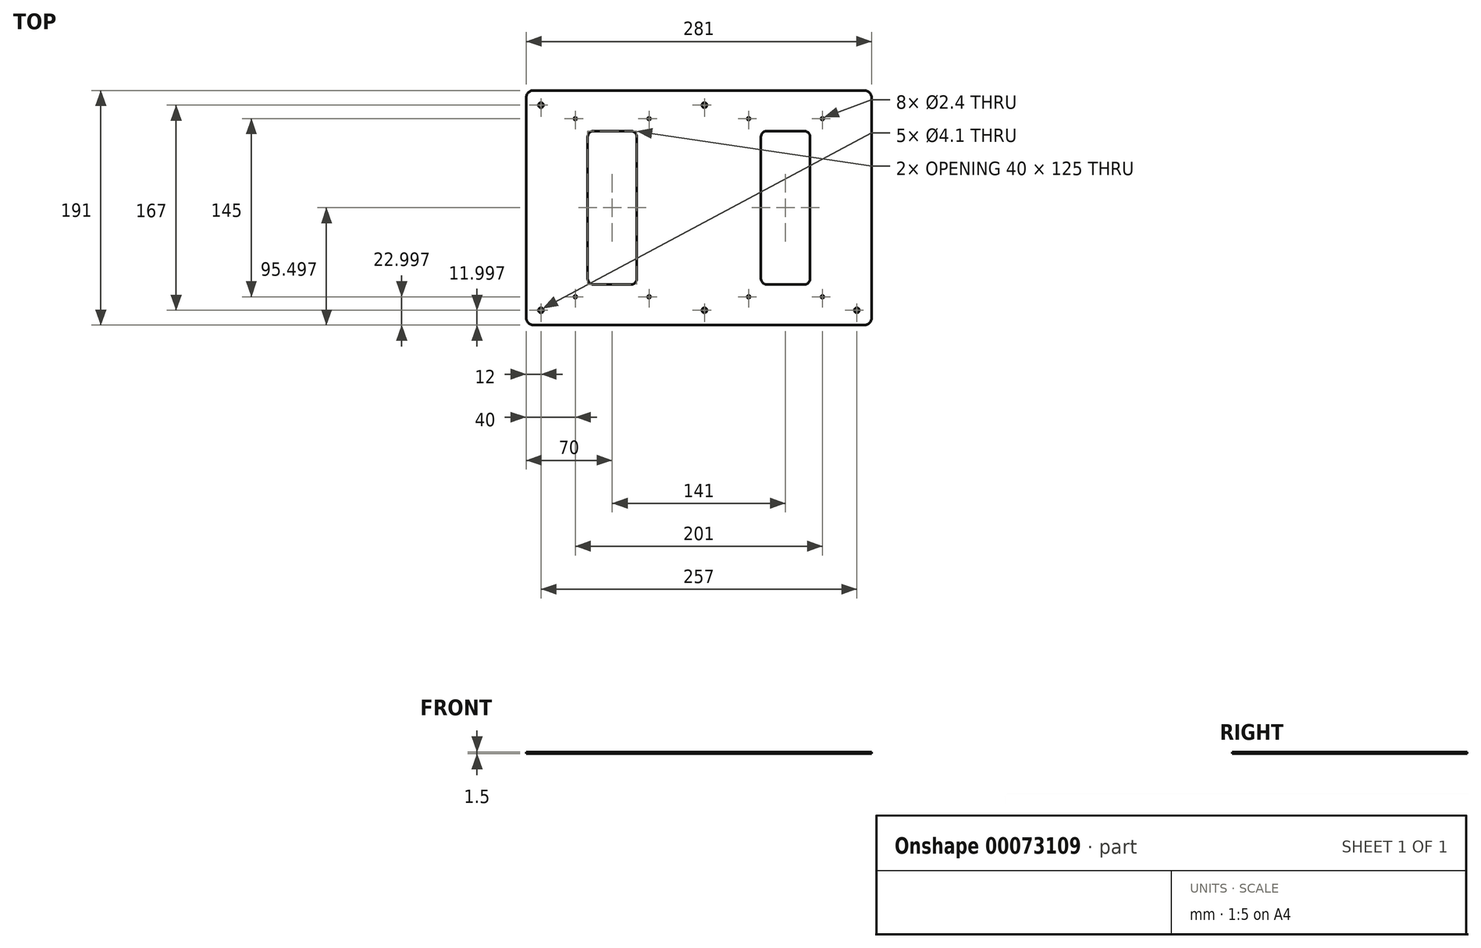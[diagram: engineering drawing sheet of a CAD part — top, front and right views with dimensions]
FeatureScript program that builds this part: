
annotation { "Feature Type Name" : "Feature", "Feature Type Description" : "" }
export const myFeature = defineFeature(function(context is Context, id is Id, definition is map)
    precondition{}
    {
        {
            var Q0;
            Q0=qCreatedBy(makeId("Top.planeOp"),FACE);
            var sketch = newSketch(context, id + "F0", { "sketchPlane" : qUnion([Q0])});
            skLineSegment(sketch, "E0.rect.bottom", {"start": v(-126, 99.25) * mm, "end": v(155, 99.25) * mm});
            skLineSegment(sketch, "E0.rect.top", {"start": v(-126, -91.75) * mm, "end": v(155, -91.75) * mm});
            skLineSegment(sketch, "E0.rect.left", {"start": v(-126, 99.25) * mm, "end": v(-126, -91.75) * mm});
            skLineSegment(sketch, "E0.rect.right", {"start": v(155, 99.25) * mm, "end": v(155, -91.75) * mm});
            skPoint(sketch, "E1", {"position": v(-114, 87.25) * mm});
            skPoint(sketch, "E2", {"position": v(19, 87.25) * mm});
            skPoint(sketch, "E3", {"position": v(143, -79.75) * mm});
            skPoint(sketch, "E4", {"position": v(-114, -79.75) * mm});
            skPoint(sketch, "E5", {"position": v(19, -79.75) * mm});
            skLineSegment(sketch, "E6", {"start": v(-126, 3.75) * mm, "end": v(155, 3.75) * mm, "construction": true});
            skPoint(sketch, "E7", {"position": v(-86, 76.25) * mm});
            skPoint(sketch, "E8", {"position": v(-86, -68.75) * mm});
            skPoint(sketch, "E9", {"position": v(-26, -68.75) * mm});
            skPoint(sketch, "E10", {"position": v(-26, 76.25) * mm});
            skLineSegment(sketch, "E11.bottom", {"start": v(-71, 66.25) * mm, "end": v(-41, 66.25) * mm});
            skLineSegment(sketch, "E11.top", {"start": v(-71, -58.75) * mm, "end": v(-41, -58.75) * mm});
            skLineSegment(sketch, "E11.left", {"start": v(-76, 61.25) * mm, "end": v(-76, -53.75) * mm});
            skLineSegment(sketch, "E11.right", {"start": v(-36, 61.25) * mm, "end": v(-36, -53.75) * mm});
            skPoint(sketch, "E12.visualSharp", {"position": v(-76, 66.25) * mm});
            skArc(sketch, "E12.filletArc", {"start": v(-71, 66.25) * mm, "mid": v(-74.54, 64.78) * mm, "end": v(-76, 61.25) * mm});
            skPoint(sketch, "E13.visualSharp", {"position": v(-36, 66.25) * mm});
            skArc(sketch, "E13.filletArc", {"start": v(-36, 61.25) * mm, "mid": v(-37.46, 64.78) * mm, "end": v(-41, 66.25) * mm});
            skPoint(sketch, "E14.visualSharp", {"position": v(-76, -58.75) * mm});
            skArc(sketch, "E14.filletArc", {"start": v(-76, -53.75) * mm, "mid": v(-74.54, -57.29) * mm, "end": v(-71, -58.75) * mm});
            skPoint(sketch, "E15.visualSharp", {"position": v(-36, -58.75) * mm});
            skArc(sketch, "E15.filletArc", {"start": v(-41, -58.75) * mm, "mid": v(-37.46, -57.29) * mm, "end": v(-36, -53.75) * mm});
            skLineSegment(sketch, "E16", {"start": v(14.5, 99.25) * mm, "end": v(14.5, -195.72) * mm, "construction": true});
            skPoint(sketch, "E17.MirrorP", {"position": v(55, -68.75) * mm});
            skPoint(sketch, "E18.MirrorP", {"position": v(115, -68.75) * mm});
            skArc(sketch, "E19.MirrorCS", {"start": v(105, -53.75) * mm, "mid": v(103.54, -57.29) * mm, "end": v(100, -58.75) * mm});
            skArc(sketch, "E20.MirrorCS", {"start": v(70, -58.75) * mm, "mid": v(66.46, -57.29) * mm, "end": v(65, -53.75) * mm});
            skPoint(sketch, "E21.MirrorP", {"position": v(105, -58.75) * mm});
            skLineSegment(sketch, "E22.MirrorCS", {"start": v(105, 61.25) * mm, "end": v(105, -53.75) * mm});
            skPoint(sketch, "E23.MirrorP", {"position": v(65, -58.75) * mm});
            skLineSegment(sketch, "E24.MirrorCS", {"start": v(65, 61.25) * mm, "end": v(65, -53.75) * mm});
            skLineSegment(sketch, "E25.MirrorCS", {"start": v(100, -58.75) * mm, "end": v(70, -58.75) * mm});
            skArc(sketch, "E26.MirrorCS", {"start": v(65, 61.25) * mm, "mid": v(66.46, 64.78) * mm, "end": v(70, 66.25) * mm});
            skArc(sketch, "E27.MirrorCS", {"start": v(100, 66.25) * mm, "mid": v(103.54, 64.78) * mm, "end": v(105, 61.25) * mm});
            skPoint(sketch, "E28.MirrorP", {"position": v(105, 66.25) * mm});
            skPoint(sketch, "E29.MirrorP", {"position": v(65, 66.25) * mm});
            skLineSegment(sketch, "E30.MirrorCS", {"start": v(100, 66.25) * mm, "end": v(70, 66.25) * mm});
            skPoint(sketch, "E31.MirrorP", {"position": v(115, 76.25) * mm});
            skPoint(sketch, "E32.MirrorP", {"position": v(55, 76.25) * mm});
            skLineSegment(sketch, "E33.trimOffspring", {"start": v(30.5, -91.75) * mm, "end": v(30.5, -195.72) * mm});
            skLineSegment(sketch, "E34.trimOffspring", {"start": v(-1.5, -91.75) * mm, "end": v(-1.5, -195.72) * mm});
            skPoint(sketch, "E35", {"position": v(-1.5, 19.75) * mm});
            skPoint(sketch, "E36", {"position": v(30.5, 19.75) * mm});
            skPoint(sketch, "E37", {"position": v(30.5, -12.25) * mm});
            skPoint(sketch, "E38", {"position": v(-1.5, -12.25) * mm});
            skPoint(sketch, "E39", {"position": v(14.5, 3.75) * mm});
            skSolve(sketch);
        }
        {
            var Q0;
            Q0=makeQuery(id+"F0.imprint","IMPRINT",FACE,{"disambiguationData":[TD([[makeQuery(id+"F0.imprint","IMPRINT",EDGE,{"derivedFrom":sQuery(id+"F0.wireOp",EDGE,"E0.rect.bottom")}),-1.0]])]});
            extrude(context, id + "F1", {"entities" : qUnion([Q0]), "depth" : 1.5 * mm});
        }
        {
            var Q0;
            Q0=sQuery(id+"F0.wireOp",VERTEX,"E1");
            var Q1;
            Q1=sQuery(id+"F0.wireOp",VERTEX,"E2");
            var Q2;
            Q2=sQuery(id+"F0.wireOp",VERTEX,"E3");
            var Q3;
            Q3=sQuery(id+"F0.wireOp",VERTEX,"E4");
            var Q4;
            Q4=sQuery(id+"F0.wireOp",VERTEX,"E5");
            var Q5;
            Q5=makeQuery(id+"F1.opExtrude","SWEPT_BODY",BODY,{"disambiguationData":[OSD([sQuery(id+"F0.wireOp",EDGE,"E0.rect.bottom"),sQuery(id+"F0.wireOp",EDGE,"E0.rect.top"),sQuery(id+"F0.wireOp",EDGE,"E0.rect.left"),sQuery(id+"F0.wireOp",EDGE,"E0.rect.right")])]});
            hole(context, id + "F2", {"style" : HoleStyle.SIMPLE, "endStyle" : HoleEndStyle.THROUGH, "oppositeDirection" : true, "standardTappedOrClearance" : lookupTablePath({ "standard" : "ISO", "size" : "4.1", "type" : "Drilled" }), "standardBlindInLast" : lookupTablePath({ "standard" : "ISO", "size" : "4.1", "type" : "Drilled" }), "holeDiameter" : 4.1 * mm, "locations" : qUnion([Q0, Q1, Q2, Q3, Q4]), "scope" : qUnion([Q5]), "isTappedThrough" : true});
        }
        {
            var Q0;
            Q0=makeQuery(id+"F1.opExtrude","SWEPT_EDGE",EDGE,{"disambiguationData":[OSD([sQuery(id+"F0.wireOp",EDGE,"E0.rect.bottom"),sQuery(id+"F0.wireOp",EDGE,"E0.rect.left")])]});
            var Q1;
            Q1=makeQuery(id+"F1.opExtrude","SWEPT_EDGE",EDGE,{"disambiguationData":[OSD([sQuery(id+"F0.wireOp",EDGE,"E0.rect.top"),sQuery(id+"F0.wireOp",EDGE,"E0.rect.left")])]});
            var Q2;
            Q2=makeQuery(id+"F1.opExtrude","SWEPT_EDGE",EDGE,{"disambiguationData":[OSD([sQuery(id+"F0.wireOp",EDGE,"E0.rect.top"),sQuery(id+"F0.wireOp",EDGE,"E0.rect.right")])]});
            var Q3;
            Q3=makeQuery(id+"F1.opExtrude","SWEPT_EDGE",EDGE,{"disambiguationData":[OSD([sQuery(id+"F0.wireOp",EDGE,"E0.rect.bottom"),sQuery(id+"F0.wireOp",EDGE,"E0.rect.right")])]});
            fillet(context, id + "F3", {"entities" : qUnion([Q0, Q1, Q2, Q3]), "radius" : 6 * mm, "tangentPropagation" : true, "allowEdgeOverflow" : false});
        }
        {
            var Q0;
            Q0=sQuery(id+"F0.wireOp",VERTEX,"E10");
            var Q1;
            Q1=sQuery(id+"F0.wireOp",VERTEX,"E7");
            var Q2;
            Q2=sQuery(id+"F0.wireOp",VERTEX,"E9");
            var Q3;
            Q3=sQuery(id+"F0.wireOp",VERTEX,"E8");
            var Q4;
            Q4=sQuery(id+"F0.wireOp",VERTEX,"E32.MirrorP");
            var Q5;
            Q5=sQuery(id+"F0.wireOp",VERTEX,"E31.MirrorP");
            var Q6;
            Q6=sQuery(id+"F0.wireOp",VERTEX,"E18.MirrorP");
            var Q7;
            Q7=sQuery(id+"F0.wireOp",VERTEX,"E17.MirrorP");
            var Q8;
            Q8=makeQuery(id+"F1.opExtrude","SWEPT_BODY",BODY,{"disambiguationData":[OSD([sQuery(id+"F0.wireOp",EDGE,"E0.rect.bottom"),sQuery(id+"F0.wireOp",EDGE,"E0.rect.top"),sQuery(id+"F0.wireOp",EDGE,"E0.rect.left"),sQuery(id+"F0.wireOp",EDGE,"E0.rect.right")])]});
            hole(context, id + "F4", {"style" : HoleStyle.SIMPLE, "endStyle" : HoleEndStyle.THROUGH, "oppositeDirection" : true, "standardTappedOrClearance" : lookupTablePath({ "standard" : "ISO", "engagement" : "75%", "pitch" : "0.6 mm", "size" : "M3", "type" : "Tapped" }), "standardBlindInLast" : lookupTablePath({ "standard" : "ISO", "engagement" : "75%", "pitch" : "0.6 mm", "size" : "M3", "type" : "Tapped" }), "holeDiameter" : 2.4 * mm, "locations" : qUnion([Q0, Q1, Q2, Q3, Q4, Q5, Q6, Q7]), "scope" : qUnion([Q8]), "isTappedThrough" : true, "showTappedDepth" : true});
        }
        {
            var Q0;
            Q0=makeQuery(id+"F1.opExtrude","SWEPT_BODY",BODY,{"disambiguationData":[OSD([sQuery(id+"F0.wireOp",EDGE,"E0.rect.bottom"),sQuery(id+"F0.wireOp",EDGE,"E0.rect.top"),sQuery(id+"F0.wireOp",EDGE,"E0.rect.left"),sQuery(id+"F0.wireOp",EDGE,"E0.rect.right"),sQuery(id+"F0.wireOp",EDGE,"E11.bottom"),sQuery(id+"F0.wireOp",EDGE,"E11.top"),sQuery(id+"F0.wireOp",EDGE,"E11.left"),sQuery(id+"F0.wireOp",EDGE,"E11.right"),sQuery(id+"F0.wireOp",EDGE,"E12.filletArc"),sQuery(id+"F0.wireOp",EDGE,"E13.filletArc"),sQuery(id+"F0.wireOp",EDGE,"E14.filletArc"),sQuery(id+"F0.wireOp",EDGE,"E15.filletArc"),sQuery(id+"F0.wireOp",EDGE,"E19.MirrorCS"),sQuery(id+"F0.wireOp",EDGE,"E20.MirrorCS"),sQuery(id+"F0.wireOp",EDGE,"E25.MirrorCS"),sQuery(id+"F0.wireOp",EDGE,"E26.MirrorCS"),sQuery(id+"F0.wireOp",EDGE,"E27.MirrorCS"),sQuery(id+"F0.wireOp",EDGE,"E22.MirrorCS"),sQuery(id+"F0.wireOp",EDGE,"E24.MirrorCS"),sQuery(id+"F0.wireOp",EDGE,"E30.MirrorCS")])]});
            transform(context, id + "F5", {"entities" : qUnion([Q0]), "transformType" : TransformType.TRANSLATION_3D, "dx" : 0 * mm, "dy" : 0 * mm, "dz" : 65 * mm, "makeCopy" : false});
        }
        {
            var Q0;
            Q0=makeQuery(id+"F1.opExtrude","SWEPT_BODY",BODY,{"disambiguationData":[OSD([sQuery(id+"F0.wireOp",EDGE,"E0.rect.bottom"),sQuery(id+"F0.wireOp",EDGE,"E0.rect.top"),sQuery(id+"F0.wireOp",EDGE,"E0.rect.left"),sQuery(id+"F0.wireOp",EDGE,"E0.rect.right"),sQuery(id+"F0.wireOp",EDGE,"E11.bottom"),sQuery(id+"F0.wireOp",EDGE,"E11.top"),sQuery(id+"F0.wireOp",EDGE,"E11.left"),sQuery(id+"F0.wireOp",EDGE,"E11.right"),sQuery(id+"F0.wireOp",EDGE,"E12.filletArc"),sQuery(id+"F0.wireOp",EDGE,"E13.filletArc"),sQuery(id+"F0.wireOp",EDGE,"E14.filletArc"),sQuery(id+"F0.wireOp",EDGE,"E15.filletArc"),sQuery(id+"F0.wireOp",EDGE,"E19.MirrorCS"),sQuery(id+"F0.wireOp",EDGE,"E20.MirrorCS"),sQuery(id+"F0.wireOp",EDGE,"E25.MirrorCS"),sQuery(id+"F0.wireOp",EDGE,"E26.MirrorCS"),sQuery(id+"F0.wireOp",EDGE,"E27.MirrorCS"),sQuery(id+"F0.wireOp",EDGE,"E22.MirrorCS"),sQuery(id+"F0.wireOp",EDGE,"E24.MirrorCS"),sQuery(id+"F0.wireOp",EDGE,"E30.MirrorCS")])]});
            transform(context, id + "F6", {"entities" : qUnion([Q0]), "transformType" : TransformType.TRANSLATION_3D, "dx" : -2 * mm, "dy" : -2 * mm, "dz" : 0 * mm, "makeCopy" : false});
        }
    });
